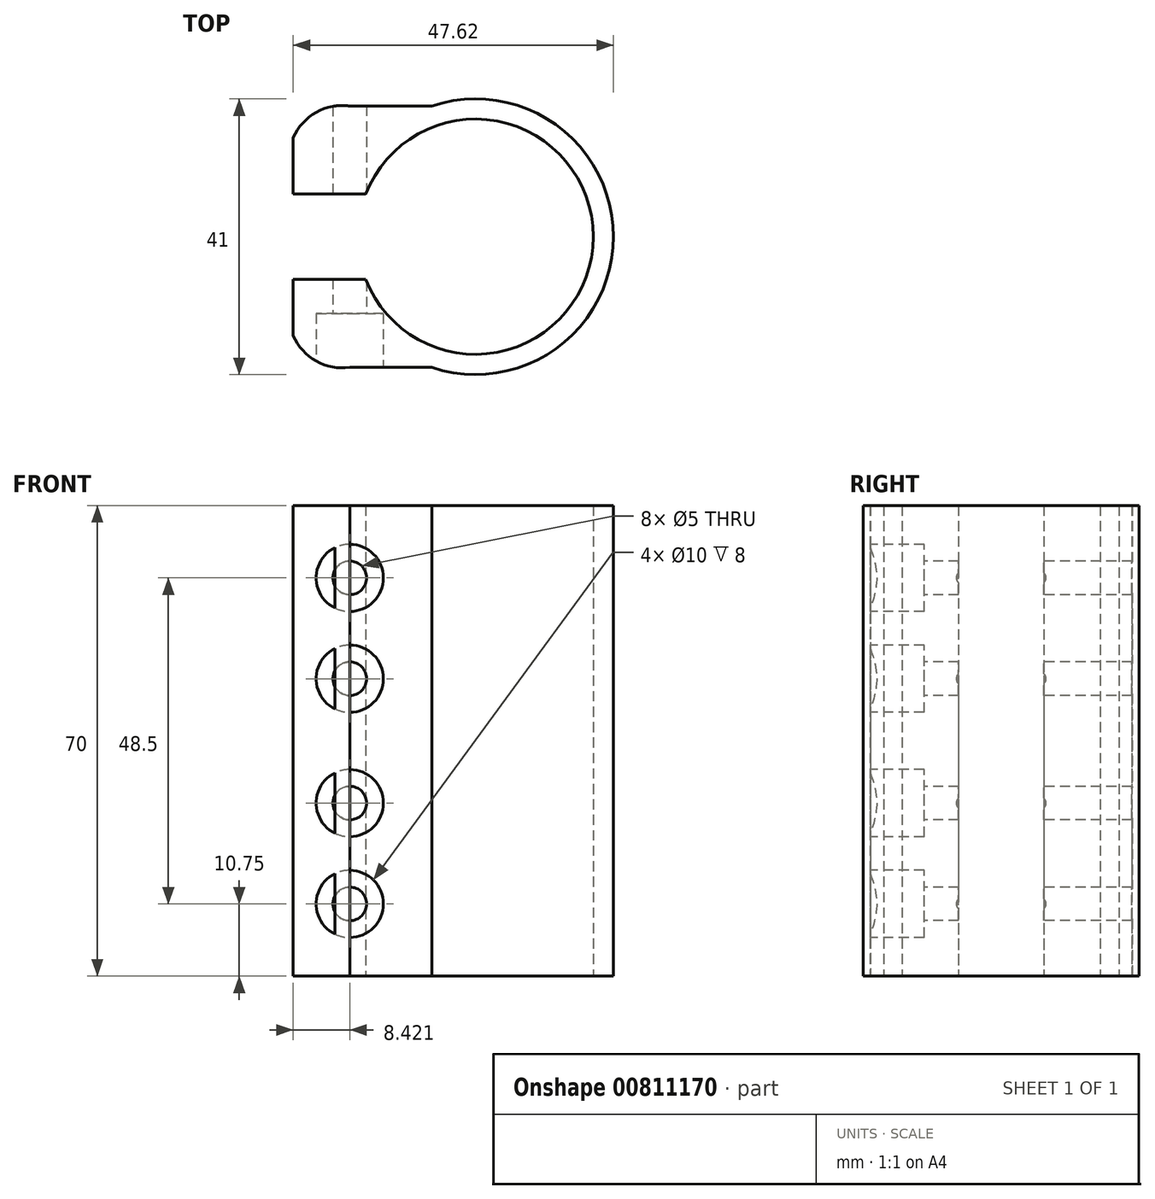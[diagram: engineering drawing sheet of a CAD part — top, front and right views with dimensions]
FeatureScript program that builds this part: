
annotation { "Feature Type Name" : "Feature", "Feature Type Description" : "" }
export const myFeature = defineFeature(function(context is Context, id is Id, definition is map)
    precondition{}
    {
        {
            var Q0;
            Q0=qCreatedBy(makeId("Top.planeOp"),FACE);
            var sketch = newSketch(context, id + "F0", { "sketchPlane" : qUnion([Q0])});
            skArc(sketch, "E0", {"start": v(-16.32, -6.33) * mm, "mid": v(17.5, 0) * mm, "end": v(-16.32, 6.33) * mm});
            skArc(sketch, "E1", {"start": v(-6.5, -19.44) * mm, "mid": v(20.5, 0) * mm, "end": v(-6.5, 19.44) * mm});
            skLineSegment(sketch, "E2", {"start": v(-19.5, 6.33) * mm, "end": v(-27.12, 6.33) * mm});
            skLineSegment(sketch, "E3", {"start": v(-27.12, 6.33) * mm, "end": v(-27.12, 14.73) * mm});
            skLineSegment(sketch, "E4", {"start": v(-19.5, 6.33) * mm, "end": v(-16.32, 6.33) * mm});
            skLineSegment(sketch, "E5", {"start": v(0, 0) * mm, "end": v(50.36, 0) * mm, "construction": true});
            skLineSegment(sketch, "E6", {"start": v(-6.5, 19.44) * mm, "end": v(-18.7, 19.44) * mm});
            skArc(sketch, "E7.filletArc", {"start": v(-18.7, 19.44) * mm, "mid": v(-23.7, 18.5) * mm, "end": v(-27.12, 14.73) * mm});
            skLineSegment(sketch, "E8.MirrorCS", {"start": v(-6.43, -19.44) * mm, "end": v(-18.7, -19.44) * mm});
            skArc(sketch, "E9.MirrorCS", {"start": v(-18.7, -19.44) * mm, "mid": v(-23.7, -18.5) * mm, "end": v(-27.12, -14.73) * mm});
            skLineSegment(sketch, "E10.MirrorCS", {"start": v(-27.12, -6.33) * mm, "end": v(-27.12, -14.73) * mm});
            skLineSegment(sketch, "E11.MirrorCS", {"start": v(-19.5, -6.33) * mm, "end": v(-27.12, -6.33) * mm});
            skLineSegment(sketch, "E12.MirrorCS", {"start": v(-19.5, -6.33) * mm, "end": v(-16.32, -6.33) * mm});
            skPoint(sketch, "E13.orphan", {"position": v(-6.5, -19.44) * mm});
            skSolve(sketch);
        }
        {
            var Q0;
            Q0=makeQuery(id+"F0.imprint","IMPRINT",FACE,{"disambiguationData":[TD([[makeQuery(id+"F0.imprint","IMPRINT",EDGE,{"derivedFrom":sQuery(id+"F0.wireOp",EDGE,"E0")}),-1.0]])]});
            extrude(context, id + "F1", {"entities" : qUnion([Q0]), "endBound" : BoundingType.SYMMETRIC, "depth" : 70 * mm, "offsetDistance" : 25 * mm});
        }
        {
            var Q0;
            Q0=makeQuery(id+"F1.opExtrude","SWEPT_FACE",FACE,{"disambiguationData":[OSD([sQuery(id+"F0.wireOp",EDGE,"E8.MirrorCS")])]});
            var sketch = newSketch(context, id + "F2", { "sketchPlane" : qUnion([Q0])});
            skPoint(sketch, "E14", {"position": v(-18.7, 24.25) * mm});
            skPoint(sketch, "E15", {"position": v(-18.7, 9.25) * mm});
            skPoint(sketch, "E16", {"position": v(-18.7, -9.25) * mm});
            skPoint(sketch, "E17", {"position": v(-18.7, -24.25) * mm});
            skSolve(sketch);
        }
        {
            var Q0;
            Q0=sQuery(id+"F2.wireOp",VERTEX,"E14");
            var Q1;
            Q1=sQuery(id+"F2.wireOp",VERTEX,"E16");
            var Q2;
            Q2=sQuery(id+"F2.wireOp",VERTEX,"E17");
            var Q3;
            Q3=sQuery(id+"F2.wireOp",VERTEX,"E15");
            var Q4;
            Q4=makeQuery(id+"F1.opExtrude","SWEPT_BODY",BODY,{"disambiguationData":[OSD([sQuery(id+"F0.wireOp",EDGE,"E0"),sQuery(id+"F0.wireOp",EDGE,"E1"),sQuery(id+"F0.wireOp",EDGE,"E2"),sQuery(id+"F0.wireOp",EDGE,"E3"),sQuery(id+"F0.wireOp",EDGE,"E4"),sQuery(id+"F0.wireOp",EDGE,"E6"),sQuery(id+"F0.wireOp",EDGE,"E7.filletArc"),sQuery(id+"F0.wireOp",EDGE,"E8.MirrorCS"),sQuery(id+"F0.wireOp",EDGE,"E9.MirrorCS"),sQuery(id+"F0.wireOp",EDGE,"E10.MirrorCS"),sQuery(id+"F0.wireOp",EDGE,"E11.MirrorCS"),sQuery(id+"F0.wireOp",EDGE,"E12.MirrorCS")])]});
            hole(context, id + "F3", {"style" : HoleStyle.C_BORE, "endStyle" : HoleEndStyle.THROUGH, "holeDiameter" : 5 * mm, "cBoreDiameter" : 10 * mm, "cBoreDepth" : 8 * mm, "majorDiameter" : 5 * mm, "isTappedThrough" : true, "tappedDepth" : 12 * mm, "tapClearance" : 3, "locations" : qUnion([Q0, Q1, Q2, Q3]), "scope" : qUnion([Q4])});
        }
    });
